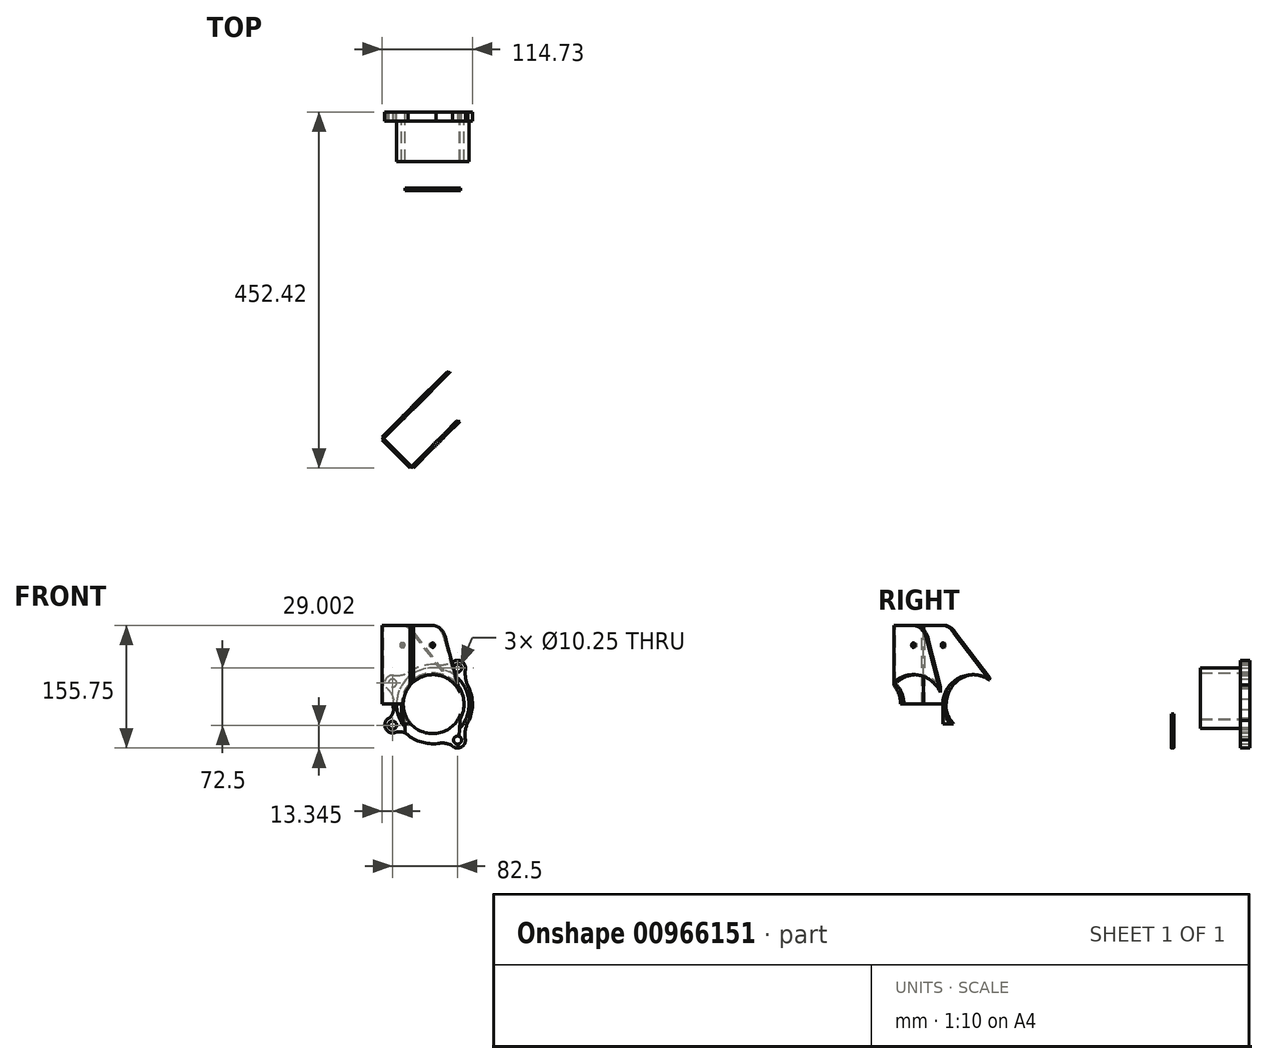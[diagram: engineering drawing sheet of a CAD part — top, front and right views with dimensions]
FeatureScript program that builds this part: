
annotation { "Feature Type Name" : "Feature", "Feature Type Description" : "" }
export const myFeature = defineFeature(function(context is Context, id is Id, definition is map)
    precondition{}
    {
        {
            var Q0;
            Q0=qCreatedBy(makeId("Front.planeOp"),FACE);
            var sketch = newSketch(context, id + "F0", { "sketchPlane" : qUnion([Q0])});
            skLineSegment(sketch, "E0", {"start": v(-45.88, 158.06) * mm, "end": v(-45.88, 92.8) * mm});
            skPoint(sketch, "E1.orphan", {"position": v(-70.88, 8.06) * mm});
            skPoint(sketch, "E2.top.start.orphan", {"position": v(-45.88, 8.06) * mm});
            skPoint(sketch, "E3.orphan", {"position": v(-20.88, 8.06) * mm});
            skLineSegment(sketch, "E4", {"start": v(-45.88, 158.06) * mm, "end": v(-45.88, 212.33) * mm, "construction": true});
            skCircle(sketch, "E5", {"center": v(-45.88, 212.33) * mm, "radius": 39.75 * mm});
            skCircle(sketch, "E6", {"center": v(-96.88, 239.08) * mm, "radius": 5.13 * mm});
            skCircle(sketch, "E7", {"center": v(-96.88, 185.58) * mm, "radius": 5.12 * mm});
            skLineSegment(sketch, "E8", {"start": v(-45.88, 212.33) * mm, "end": v(-96.88, 212.33) * mm, "construction": true});
            skCircle(sketch, "E9", {"center": v(-14.38, 258.08) * mm, "radius": 5.12 * mm});
            skCircle(sketch, "E10", {"center": v(-14.38, 166.58) * mm, "radius": 5.12 * mm});
            skLineSegment(sketch, "E11", {"start": v(-45.88, 212.33) * mm, "end": v(-14.38, 212.33) * mm, "construction": true});
            skLineSegment(sketch, "E12", {"start": v(-96.88, 239.08) * mm, "end": v(-96.88, 185.58) * mm, "construction": true});
            skLineSegment(sketch, "E13", {"start": v(-14.38, 258.08) * mm, "end": v(-14.38, 166.58) * mm, "construction": true});
            skCircle(sketch, "E14", {"center": v(-45.88, 212.33) * mm, "radius": 37.5 * mm});
            skCircle(sketch, "E15", {"center": v(-45.88, 212.33) * mm, "radius": 36 * mm});
            skArc(sketch, "E16", {"start": v(-4.44, 256.92) * mm, "mid": v(-9.67, 266.9) * mm, "end": v(-20.88, 265.68) * mm});
            skArc(sketch, "E17", {"start": v(-95.78, 249.02) * mm, "mid": v(-105.75, 243.7) * mm, "end": v(-104.38, 232.48) * mm});
            skArc(sketch, "E18", {"start": v(-101.31, 194.54) * mm, "mid": v(-105.87, 181.22) * mm, "end": v(-92.6, 176.55) * mm});
            skArc(sketch, "E19", {"start": v(-21.82, 159.91) * mm, "mid": v(-9.65, 157.77) * mm, "end": v(-4.7, 169.09) * mm});
            skArc(sketch, "E20", {"start": v(-39.34, 262.3) * mm, "mid": v(-59.48, 260.85) * mm, "end": v(-77.44, 251.6) * mm});
            skArc(sketch, "E21.trimOffspring", {"start": v(-95.78, 219.27) * mm, "mid": v(-96.26, 212.33) * mm, "end": v(-95.78, 205.4) * mm});
            skArc(sketch, "E22.trimOffspring", {"start": v(-78.83, 174.21) * mm, "mid": v(-59.11, 163.72) * mm, "end": v(-36.8, 162.77) * mm});
            skArc(sketch, "E23.trimOffspring", {"start": v(-2.07, 187.43) * mm, "mid": v(4.51, 212.12) * mm, "end": v(-1.86, 236.86) * mm});
            skArc(sketch, "E24", {"start": v(-4.44, 256.92) * mm, "mid": v(-4.39, 246.73) * mm, "end": v(-1.86, 236.86) * mm});
            skArc(sketch, "E25", {"start": v(0, 191.5) * mm, "mid": v(-4.4, 179.69) * mm, "end": v(-4.39, 167.09) * mm});
            skArc(sketch, "E26", {"start": v(-21.82, 159.91) * mm, "mid": v(-30.43, 162.66) * mm, "end": v(-39.45, 162.36) * mm});
            skArc(sketch, "E27", {"start": v(-78.83, 174.21) * mm, "mid": v(-85.42, 177.1) * mm, "end": v(-92.6, 176.55) * mm});
            skArc(sketch, "E28", {"start": v(-101.31, 194.54) * mm, "mid": v(-97.46, 199.42) * mm, "end": v(-95.78, 205.4) * mm});
            skArc(sketch, "E29", {"start": v(-95.78, 219.27) * mm, "mid": v(-98.85, 226.67) * mm, "end": v(-104.38, 232.48) * mm});
            skArc(sketch, "E30", {"start": v(-95.78, 249.02) * mm, "mid": v(-86.45, 249.18) * mm, "end": v(-77.44, 251.6) * mm});
            skArc(sketch, "E31", {"start": v(-41.62, 262.54) * mm, "mid": v(-31.02, 262.6) * mm, "end": v(-20.88, 265.68) * mm});
            skCircle(sketch, "E32", {"center": v(-45.88, 212.33) * mm, "radius": 46 * mm});
            skLineSegment(sketch, "E33", {"start": v(-45.88, 174.83) * mm, "end": v(-45.88, 124.83) * mm});
            skCircle(sketch, "E34", {"center": v(-45.88, 124.83) * mm, "radius": 6 * mm});
            skPoint(sketch, "E35.center.orphan", {"position": v(-45.88, 113.06) * mm});
            skLineSegment(sketch, "E36", {"start": v(-70.88, 181.43) * mm, "end": v(-70.88, 184.38) * mm});
            skLineSegment(sketch, "E37", {"start": v(-20.88, 158.06) * mm, "end": v(-20.88, 158.98) * mm});
            skLineSegment(sketch, "E38", {"start": v(-45.88, 124.83) * mm, "end": v(-45.88, 99.83) * mm});
            skPoint(sketch, "E39.center.orphan", {"position": v(-45.88, 88.06) * mm});
            skCircle(sketch, "E40", {"center": v(-45.88, 99.83) * mm, "radius": 6 * mm});
            skLineSegment(sketch, "E41", {"start": v(-45.88, 99.83) * mm, "end": v(-45.88, 92.8) * mm});
            skCircle(sketch, "E42", {"center": v(-45.88, 74.83) * mm, "radius": 6 * mm});
            skArc(sketch, "E43", {"start": v(-45.88, 49.83) * mm, "mid": v(-28.2, 57.15) * mm, "end": v(-20.88, 74.83) * mm});
            skLineSegment(sketch, "E44", {"start": v(-45.88, 124.83) * mm, "end": v(-80.88, 124.83) * mm});
            skLineSegment(sketch, "E45", {"start": v(-80.88, 124.83) * mm, "end": v(-80.88, 74.83) * mm});
            skLineSegment(sketch, "E46", {"start": v(-80.88, 124.83) * mm, "end": v(-80.88, 198.87) * mm});
            skPoint(sketch, "E2.left.start.orphan", {"position": v(-70.88, 158.06) * mm});
            skLineSegment(sketch, "E47", {"start": v(-55.88, 49.83) * mm, "end": v(-45.88, 49.83) * mm});
            skLineSegment(sketch, "E48", {"start": v(-45.88, 49.83) * mm, "end": v(-55.88, 49.83) * mm});
            skArc(sketch, "E49", {"start": v(-80.88, 74.83) * mm, "mid": v(-73.55, 57.15) * mm, "end": v(-55.88, 49.83) * mm});
            skLineSegment(sketch, "E50.trimOffspring", {"start": v(-45.88, 80.83) * mm, "end": v(-45.88, 74.83) * mm});
            skLineSegment(sketch, "E51.trimOffspring", {"start": v(-45.88, 88.06) * mm, "end": v(-45.88, 74.83) * mm});
            skLineSegment(sketch, "E52", {"start": v(-10.45, 200.03) * mm, "end": v(-20.88, 74.83) * mm});
            skLineSegment(sketch, "E53.trimOffspring", {"start": v(-20.88, 181.43) * mm, "end": v(-20.88, 184.38) * mm});
            skSolve(sketch);
        }
        {
            var Q0;
            Q0=makeQuery(id+"F0.imprint","IMPRINT",FACE,{"disambiguationData":[TD([[makeQuery(id+"F0.imprint","IMPRINT",EDGE,{"derivedFrom":sQuery(id+"F0.wireOp",EDGE,"E14")}),1.0]])]});
            extrude(context, id + "F1", {"entities" : qUnion([Q0]), "depth" : 400 * mm, "offsetDistance" : 25 * mm});
        }
        {
            var Q0;
            Q0=sQuery(id+"F0.wireOp",VERTEX,"E4.end");
            var Q1;
            Q1=sQuery(id+"F0.wireOp",EDGE,"E11");
            cPlane(context, id + "F2", {"entities" : qUnion([Q0, Q1]), "cplaneType" : CPlaneType.LINE_POINT, "offset" : 25 * mm, "width" : 150 * mm, "height" : 150 * mm});
        }
        {
            var Q0;
            Q0=qCreatedBy(id+"F2.planeOp",FACE);
            var sketch = newSketch(context, id + "F3", { "sketchPlane" : qUnion([Q0])});
            skLineSegment(sketch, "E54", {"start": v(0, 212.33) * mm, "end": v(-611, 212.33) * mm});
            skCircle(sketch, "E55", {"center": v(-611, 212.33) * mm, "radius": 66.24 * mm});
            skLineSegment(sketch, "E56", {"start": v(-427.67, 212.33) * mm, "end": v(-427.67, 287.33) * mm});
            skLineSegment(sketch, "E57", {"start": v(-395.17, 281.83) * mm, "end": v(-395.17, 235.86) * mm});
            skLineSegment(sketch, "E58", {"start": v(-427.67, 212.33) * mm, "end": v(-427.67, 249.83) * mm});
            skLineSegment(sketch, "E59", {"start": v(-427.67, 249.83) * mm, "end": v(-370.95, 249.83) * mm});
            skLineSegment(sketch, "E60", {"start": v(-427.67, 249.83) * mm, "end": v(-427.67, 281.83) * mm});
            skLineSegment(sketch, "E61", {"start": v(-427.67, 281.83) * mm, "end": v(-395.17, 281.83) * mm});
            skSolve(sketch);
        }
        {
            var Q0;
            Q0=makeQuery(id+"F0.imprint","IMPRINT",FACE,{"disambiguationData":[TD([[makeQuery(id+"F0.imprint","IMPRINT",EDGE,{"derivedFrom":sQuery(id+"F0.wireOp",EDGE,"E6")}),-1.0]])]});
            var Q1;
            {var subQ1=sQuery(id+"F0.wireOp",EDGE,"E22.trimOffspring");var subQ7=sQuery(id+"F0.wireOp",EDGE,"E27");var subQ8=makeQuery(id+"F0.imprint","INTERSECT",VERTEX,{"derivedFrom":[subQ1,subQ7]});Q1=makeQuery(id+"F0.imprint","IMPRINT",FACE,{"disambiguationData":[TD([[makeQuery(id+"F0.imprint","IMPRINT",EDGE,{"disambiguationData":[TD([[subQ8,-1.0]])],"derivedFrom":subQ1}),1.0]])]});}
            var Q2;
            {var subQ7=sQuery(id+"F0.wireOp",EDGE,"E19");var subQ8=makeQuery(id+"F0.imprint","IMPRINT",VERTEX,{"derivedFrom":subQ7});Q2=makeQuery(id+"F0.imprint","IMPRINT",FACE,{"disambiguationData":[TD([[makeQuery(id+"F0.imprint","IMPRINT",EDGE,{"disambiguationData":[TD([[subQ8,1.0]])],"derivedFrom":subQ7}),1.0]])]});}
            extrude(context, id + "F4", {"entities" : qUnion([Q0, Q1, Q2]), "depth" : 12 * mm, "offsetDistance" : 25 * mm});
        }
        {
            var Q0;
            Q0=makeQuery(id+"F0.imprint","IMPRINT",FACE,{"disambiguationData":[TD([[makeQuery(id+"F0.imprint","IMPRINT",EDGE,{"derivedFrom":sQuery(id+"F0.wireOp",EDGE,"E14")}),1.0]])]});
            extrude(context, id + "F5", {"entities" : qUnion([Q0]), "operationType" : NewBodyOperationType.REMOVE, "depth" : 136 * mm, "offsetDistance" : 25 * mm});
        }
        {
            var Q0;
            Q0=makeQuery(id+"F0.imprint","IMPRINT",FACE,{"disambiguationData":[TD([[makeQuery(id+"F0.imprint","IMPRINT",EDGE,{"derivedFrom":sQuery(id+"F0.wireOp",EDGE,"E5")}),-1.0]])]});
            var Q1;
            {var subQ0=sQuery(id+"F0.wireOp",EDGE,"E46");var subQ1=sQuery(id+"F0.wireOp",EDGE,"E5");var subQ2=makeQuery(id+"F0.imprint","INTERSECT",VERTEX,{"derivedFrom":[subQ1,subQ0]});Q1=makeQuery(id+"F0.imprint","IMPRINT",FACE,{"disambiguationData":[TD([[makeQuery(id+"F0.imprint","IMPRINT",EDGE,{"disambiguationData":[TD([[subQ2,1.0]])],"derivedFrom":subQ1}),-1.0]])]});}
            extrude(context, id + "F6", {"entities" : qUnion([Q0, Q1]), "depth" : 63 * mm, "offsetDistance" : 25 * mm});
        }
        {
            var Q0;
            Q0=makeQuery(id+"F6.opExtrude","CAP_FACE",FACE,{"disambiguationData":[OSD([sQuery(id+"F0.wireOp",EDGE,"E5"),sQuery(id+"F0.wireOp",EDGE,"E32")])],"isStart":true});
            extrude(context, id + "F7", {"entities" : qUnion([Q0]), "operationType" : NewBodyOperationType.REMOVE, "oppositeDirection" : true, "depth" : 12 * mm, "offsetDistance" : 25 * mm});
        }
        {
            var Q0;
            Q0=sQuery(id+"F3.wireOp",EDGE,"E56");
            var Q1;
            Q1=sQuery(id+"F3.wireOp",VERTEX,"E56.end");
            cPlane(context, id + "F8", {"entities" : qUnion([Q0, Q1]), "cplaneType" : CPlaneType.LINE_POINT, "offset" : 25 * mm, "width" : 150 * mm, "height" : 150 * mm});
        }
        {
            var Q0;
            Q0=qCreatedBy(id+"F8.planeOp",FACE);
            var sketch = newSketch(context, id + "F9", { "sketchPlane" : qUnion([Q0])});
            skLineSegment(sketch, "E62", {"start": v(-45.88, -427.67) * mm, "end": v(-7.54, -427.67) * mm});
            skLineSegment(sketch, "E63", {"start": v(-45.88, -427.67) * mm, "end": v(-45.88, -449.04) * mm});
            skLineSegment(sketch, "E64", {"start": v(-45.88, -427.67) * mm, "end": v(-33.51, -440.03) * mm});
            skLineSegment(sketch, "E65", {"start": v(-48, -425.55) * mm, "end": v(-83.35, -390.2) * mm});
            skLineSegment(sketch, "E66", {"start": v(-83.35, -390.2) * mm, "end": v(-47.41, -354.25) * mm});
            skLineSegment(sketch, "E67", {"start": v(-47.41, -354.25) * mm, "end": v(-83.35, -390.2) * mm});
            skLineSegment(sketch, "E68", {"start": v(-85.47, -388.07) * mm, "end": v(6.45, -296.14) * mm});
            skLineSegment(sketch, "E69", {"start": v(-47.41, -354.25) * mm, "end": v(8.57, -298.27) * mm});
            skLineSegment(sketch, "E70", {"start": v(-48, -425.55) * mm, "end": v(22.71, -354.83) * mm});
            skLineSegment(sketch, "E71", {"start": v(-83.35, -390.2) * mm, "end": v(-12.64, -319.48) * mm});
            skLineSegment(sketch, "E72", {"start": v(-12.64, -319.48) * mm, "end": v(22.71, -354.83) * mm});
            skLineSegment(sketch, "E73", {"start": v(46.04, -335.73) * mm, "end": v(43.92, -333.61) * mm});
            skLineSegment(sketch, "E74", {"start": v(22.7, -354.83) * mm, "end": v(43.92, -333.61) * mm});
            skLineSegment(sketch, "E75", {"start": v(46.04, -335.73) * mm, "end": v(6.45, -296.14) * mm});
            skLineSegment(sketch, "E76", {"start": v(-45.88, -427.67) * mm, "end": v(-48, -425.55) * mm});
            skLineSegment(sketch, "E77.trimOffspring", {"start": v(-83.35, -390.2) * mm, "end": v(-85.47, -388.07) * mm});
            skPoint(sketch, "E78.end.orphan", {"position": v(-58.24, -440.03) * mm});
            skLineSegment(sketch, "E79", {"start": v(-45.88, -427.67) * mm, "end": v(46.04, -335.73) * mm});
            skLineSegment(sketch, "E80", {"start": v(-85.47, -388.07) * mm, "end": v(-110.22, -412.82) * mm});
            skLineSegment(sketch, "E81", {"start": v(-110.22, -412.82) * mm, "end": v(-108.1, -414.94) * mm});
            skLineSegment(sketch, "E82", {"start": v(-108.1, -414.94) * mm, "end": v(-83.35, -390.2) * mm});
            skLineSegment(sketch, "E83", {"start": v(-48, -425.55) * mm, "end": v(-72.74, -450.3) * mm});
            skLineSegment(sketch, "E84", {"start": v(-72.74, -450.3) * mm, "end": v(-70.62, -452.42) * mm});
            skLineSegment(sketch, "E85", {"start": v(-70.62, -452.42) * mm, "end": v(-45.88, -427.67) * mm});
            skLineSegment(sketch, "E86", {"start": v(-72.74, -450.3) * mm, "end": v(-108.1, -414.94) * mm});
            skLineSegment(sketch, "E87", {"start": v(-108.1, -414.94) * mm, "end": v(-110.22, -417.06) * mm});
            skLineSegment(sketch, "E88", {"start": v(-72.74, -450.3) * mm, "end": v(-74.86, -452.42) * mm});
            skLineSegment(sketch, "E89", {"start": v(-74.86, -452.42) * mm, "end": v(-110.22, -417.06) * mm});
            skSolve(sketch);
        }
        {
            var Q0;
            {var subQ4=sQuery(id+"F9.wireOp",EDGE,"E68");Q0=makeQuery(id+"F9.imprint","IMPRINT",FACE,{"disambiguationData":[TD([[makeQuery(id+"F9.imprint","IMPRINT",EDGE,{"derivedFrom":subQ4}),-1.0]])]});}
            var Q1;
            {var subQ4=sQuery(id+"F9.wireOp",EDGE,"E70");Q1=makeQuery(id+"F9.imprint","IMPRINT",FACE,{"disambiguationData":[TD([[makeQuery(id+"F9.imprint","IMPRINT",EDGE,{"derivedFrom":subQ4}),-1.0]])]});}
            extrude(context, id + "F10", {"entities" : qUnion([Q0, Q1]), "oppositeDirection" : true, "depth" : 100 * mm, "offsetDistance" : 25 * mm});
        }
        {
            var Q0;
            Q0=makeQuery(id+"F10.opExtrude","SWEPT_FACE",FACE,{"disambiguationData":[OSD([sQuery(id+"F9.wireOp",EDGE,"E74")])]});
            var sketch = newSketch(context, id + "F11", { "sketchPlane" : qUnion([Q0])});
            skLineSegment(sketch, "E90", {"start": v(234.84, 287.33) * mm, "end": v(234.84, 257.33) * mm});
            skCircle(sketch, "E91", {"center": v(234.84, 257.33) * mm, "radius": 7 * mm});
            skLineSegment(sketch, "E92", {"start": v(234.84, 257.33) * mm, "end": v(234.84, 287.33) * mm});
            skLineSegment(sketch, "E93", {"start": v(234.84, 287.33) * mm, "end": v(334.84, 287.33) * mm});
            skLineSegment(sketch, "E94", {"start": v(204.84, 247.6) * mm, "end": v(19.25, 190.9) * mm});
            skCircle(sketch, "E95", {"center": v(234.84, 257.33) * mm, "radius": 25 * mm});
            skLineSegment(sketch, "E96", {"start": v(245.66, 279.87) * mm, "end": v(334.84, 249.83) * mm});
            skLineSegment(sketch, "E97", {"start": v(290.93, 187.33) * mm, "end": v(204.84, 187.33) * mm});
            skLineSegment(sketch, "E98", {"start": v(334.84, 249.83) * mm, "end": v(334.84, 287.33) * mm});
            skLineSegment(sketch, "E99", {"start": v(221.99, 235.9) * mm, "end": v(290.93, 187.33) * mm});
            skLineSegment(sketch, "E100", {"start": v(204.84, 187.33) * mm, "end": v(204.84, 287.33) * mm});
            skLineSegment(sketch, "E101", {"start": v(204.84, 287.33) * mm, "end": v(334.84, 287.33) * mm});
            skSolve(sketch);
        }
        {
            var Q0;
            {var subQ9=sQuery(id+"F11.wireOp",EDGE,"E100");var subQ13=makeQuery(id+"F11.imprint","IMPRINT",VERTEX,{"derivedFrom":subQ9});Q0=makeQuery(id+"F11.imprint","IMPRINT",FACE,{"disambiguationData":[TD([[makeQuery(id+"F11.imprint","IMPRINT",EDGE,{"disambiguationData":[TD([[subQ13,1.0]])],"derivedFrom":subQ9}),-1.0]])]});}
            var Q1;
            {var subQ0=sQuery(id+"F11.wireOp",EDGE,"E97");var subQ1=sQuery(id+"F11.wireOp",EDGE,"E99");var subQ2=makeQuery(id+"F11.imprint","INTERSECT",VERTEX,{"derivedFrom":[subQ1,subQ0]});Q1=makeQuery(id+"F11.imprint","IMPRINT",FACE,{"disambiguationData":[TD([[makeQuery(id+"F11.imprint","IMPRINT",EDGE,{"disambiguationData":[TD([[subQ2,1.0]])],"derivedFrom":subQ1}),-1.0]])]});}
            var Q2;
            {var subQ1=sQuery(id+"F11.wireOp",EDGE,"E96");Q2=makeQuery(id+"F11.imprint","IMPRINT",FACE,{"disambiguationData":[TD([[makeQuery(id+"F11.imprint","IMPRINT",EDGE,{"derivedFrom":subQ1}),1.0]])]});}
            extrude(context, id + "F12", {"entities" : qUnion([Q0, Q1, Q2]), "operationType" : NewBodyOperationType.REMOVE, "depth" : 80.2 * mm, "offsetDistance" : 25 * mm});
        }
        {
            var Q0;
            {var subQ9=sQuery(id+"F11.wireOp",EDGE,"E100");var subQ13=makeQuery(id+"F11.imprint","IMPRINT",VERTEX,{"derivedFrom":subQ9});Q0=makeQuery(id+"F11.imprint","IMPRINT",FACE,{"disambiguationData":[TD([[makeQuery(id+"F11.imprint","IMPRINT",EDGE,{"disambiguationData":[TD([[subQ13,1.0]])],"derivedFrom":subQ9}),-1.0]])]});}
            var Q1;
            {var subQ0=sQuery(id+"F11.wireOp",EDGE,"E97");var subQ1=sQuery(id+"F11.wireOp",EDGE,"E99");var subQ2=makeQuery(id+"F11.imprint","INTERSECT",VERTEX,{"derivedFrom":[subQ1,subQ0]});Q1=makeQuery(id+"F11.imprint","IMPRINT",FACE,{"disambiguationData":[TD([[makeQuery(id+"F11.imprint","IMPRINT",EDGE,{"disambiguationData":[TD([[subQ2,1.0]])],"derivedFrom":subQ1}),-1.0]])]});}
            var Q2;
            {var subQ1=sQuery(id+"F11.wireOp",EDGE,"E96");Q2=makeQuery(id+"F11.imprint","IMPRINT",FACE,{"disambiguationData":[TD([[makeQuery(id+"F11.imprint","IMPRINT",EDGE,{"derivedFrom":subQ1}),1.0]])]});}
            extrude(context, id + "F13", {"entities" : qUnion([Q0, Q1, Q2]), "operationType" : NewBodyOperationType.REMOVE, "oppositeDirection" : true, "depth" : 25 * mm, "offsetDistance" : 25 * mm});
        }
        {
            var Q0;
            {var subQ0=sQuery(id+"F11.wireOp",EDGE,"E92");var subQ1=sQuery(id+"F11.wireOp",EDGE,"E91");var subQ2=makeQuery(id+"F11.imprint","INTERSECT",VERTEX,{"derivedFrom":[subQ1,subQ0]});Q0=makeQuery(id+"F11.imprint","IMPRINT",FACE,{"disambiguationData":[TD([[makeQuery(id+"F11.imprint","IMPRINT",EDGE,{"disambiguationData":[TD([[subQ2,1.0]])],"derivedFrom":subQ1}),1.0]])]});}
            var Q1;
            {var subQ0=sQuery(id+"F11.wireOp",EDGE,"E92");var subQ1=sQuery(id+"F11.wireOp",EDGE,"E91");var subQ2=makeQuery(id+"F11.imprint","INTERSECT",VERTEX,{"derivedFrom":[subQ1,subQ0]});Q1=makeQuery(id+"F11.imprint","IMPRINT",FACE,{"disambiguationData":[TD([[makeQuery(id+"F11.imprint","IMPRINT",EDGE,{"disambiguationData":[TD([[subQ2,-1.0]])],"derivedFrom":subQ1}),1.0]])]});}
            var Q2;
            Q2=sQuery(id+"F11.wireOp",EDGE,"E91");
            extrude(context, id + "F14", {"entities" : qUnion([Q0, Q1]), "operationType" : NewBodyOperationType.REMOVE, "surfaceEntities" : qUnion([Q2]), "depth" : 58.2 * mm, "offsetDistance" : 25 * mm});
        }
        {
            var Q0;
            {var subQ0=sQuery(id+"F11.wireOp",EDGE,"E92");var subQ1=sQuery(id+"F11.wireOp",EDGE,"E91");var subQ2=makeQuery(id+"F11.imprint","INTERSECT",VERTEX,{"derivedFrom":[subQ1,subQ0]});Q0=makeQuery(id+"F11.imprint","IMPRINT",FACE,{"disambiguationData":[TD([[makeQuery(id+"F11.imprint","IMPRINT",EDGE,{"disambiguationData":[TD([[subQ2,-1.0]])],"derivedFrom":subQ1}),1.0]])]});}
            var Q1;
            {var subQ0=sQuery(id+"F11.wireOp",EDGE,"E92");var subQ1=sQuery(id+"F11.wireOp",EDGE,"E91");var subQ2=makeQuery(id+"F11.imprint","INTERSECT",VERTEX,{"derivedFrom":[subQ1,subQ0]});Q1=makeQuery(id+"F11.imprint","IMPRINT",FACE,{"disambiguationData":[TD([[makeQuery(id+"F11.imprint","IMPRINT",EDGE,{"disambiguationData":[TD([[subQ2,1.0]])],"derivedFrom":subQ1}),1.0]])]});}
            extrude(context, id + "F15", {"entities" : qUnion([Q0, Q1]), "operationType" : NewBodyOperationType.REMOVE, "oppositeDirection" : true, "depth" : 25 * mm, "offsetDistance" : 25 * mm});
        }
        {
            var Q0;
            Q0=makeQuery(id+"F0.imprint","IMPRINT",FACE,{"disambiguationData":[TD([[makeQuery(id+"F0.imprint","IMPRINT",EDGE,{"derivedFrom":sQuery(id+"F0.wireOp",EDGE,"E14")}),1.0]])]});
            var Q1;
            Q1=sQuery(id+"F0.wireOp",EDGE,"E15");
            var Q2;
            Q2=sQuery(id+"F0.wireOp",EDGE,"E14");
            extrude(context, id + "F16", {"entities" : qUnion([Q0]), "operationType" : NewBodyOperationType.REMOVE, "surfaceEntities" : qUnion([Q1, Q2]), "depth" : 641 * mm, "offsetDistance" : 25 * mm});
        }
        {
            var Q0;
            {var subQ0=sQuery(id+"F9.wireOp",EDGE,"E71");var subQ1=sQuery(id+"F9.wireOp",EDGE,"E69");Q0=makeQuery(id+"F16.boolean.opBoolean","SPLIT",FACE,{"disambiguationData":[TD([makeQuery(id+"F10.opExtrude","CAP_FACE",FACE,{"disambiguationData":[OSD([sQuery(id+"F9.wireOp",EDGE,"E68"),subQ1,subQ0,sQuery(id+"F9.wireOp",EDGE,"E75"),sQuery(id+"F9.wireOp",EDGE,"E77.trimOffspring")])],"isStart":false}),makeQuery(id+"F12.boolean.opBoolean","COPY",FACE,{"derivedFrom":makeQuery(id+"F12.opExtrude","SWEPT_FACE",FACE,{"disambiguationData":[OSD([sQuery(id+"F11.wireOp",EDGE,"E99")])]})}),makeQuery(id+"F16.opExtrude","SWEPT_FACE",FACE,{"disambiguationData":[OSD([sQuery(id+"F0.wireOp",EDGE,"E15")])]})])],"derivedFrom":makeQuery(id+"F10.opExtrude","SWEPT_FACE",FACE,{"disambiguationData":[OSD([subQ1,subQ0])]})});}
            extrude(context, id + "F17", {"entities" : qUnion([Q0]), "operationType" : NewBodyOperationType.REMOVE, "oppositeDirection" : true, "depth" : 25 * mm, "offsetDistance" : 25 * mm});
        }
        {
            var Q0;
            Q0=makeQuery(id+"F0.imprint","IMPRINT",FACE,{"disambiguationData":[TD([[makeQuery(id+"F0.imprint","IMPRINT",EDGE,{"derivedFrom":sQuery(id+"F0.wireOp",EDGE,"E15")}),1.0]])]});
            extrude(context, id + "F18", {"entities" : qUnion([Q0]), "operationType" : NewBodyOperationType.REMOVE, "depth" : 770 * mm, "offsetDistance" : 25 * mm});
        }
        {
            var Q0;
            Q0=makeQuery(id+"F9.imprint","IMPRINT",FACE,{"disambiguationData":[TD([[makeQuery(id+"F9.imprint","IMPRINT",EDGE,{"derivedFrom":sQuery(id+"F9.wireOp",EDGE,"E86")}),1.0]])]});
            var Q1;
            Q1=makeQuery(id+"F9.imprint","IMPRINT",FACE,{"disambiguationData":[TD([[makeQuery(id+"F9.imprint","IMPRINT",EDGE,{"derivedFrom":sQuery(id+"F9.wireOp",EDGE,"E76")}),1.0]])]});
            var Q2;
            Q2=makeQuery(id+"F9.imprint","IMPRINT",FACE,{"disambiguationData":[TD([[makeQuery(id+"F9.imprint","IMPRINT",EDGE,{"derivedFrom":sQuery(id+"F9.wireOp",EDGE,"E77.trimOffspring")}),1.0]])]});
            var Q3;
            {var subQ4=sQuery(id+"F9.wireOp",EDGE,"E68");Q3=makeQuery(id+"F9.imprint","IMPRINT",FACE,{"disambiguationData":[TD([[makeQuery(id+"F9.imprint","IMPRINT",EDGE,{"derivedFrom":subQ4}),-1.0]])]});}
            var Q4;
            {var subQ4=sQuery(id+"F9.wireOp",EDGE,"E70");Q4=makeQuery(id+"F9.imprint","IMPRINT",FACE,{"disambiguationData":[TD([[makeQuery(id+"F9.imprint","IMPRINT",EDGE,{"derivedFrom":subQ4}),-1.0]])]});}
            extrude(context, id + "F19", {"entities" : qUnion([Q0, Q1, Q2, Q3, Q4]), "oppositeDirection" : true, "depth" : 75 * mm, "offsetDistance" : 25 * mm});
        }
        {
            var Q0;
            Q0=makeQuery(id+"F0.imprint","IMPRINT",FACE,{"disambiguationData":[TD([[makeQuery(id+"F0.imprint","IMPRINT",EDGE,{"derivedFrom":sQuery(id+"F0.wireOp",EDGE,"E14")}),1.0]])]});
            var Q1;
            Q1=makeQuery(id+"F0.imprint","IMPRINT",FACE,{"disambiguationData":[TD([[makeQuery(id+"F0.imprint","IMPRINT",EDGE,{"derivedFrom":sQuery(id+"F0.wireOp",EDGE,"E15")}),1.0]])]});
            extrude(context, id + "F20", {"entities" : qUnion([Q0, Q1]), "operationType" : NewBodyOperationType.REMOVE, "depth" : 487 * mm, "offsetDistance" : 25 * mm});
        }
        {
            var Q0;
            Q0=makeQuery(id+"F9.imprint","IMPRINT",FACE,{"disambiguationData":[TD([[makeQuery(id+"F9.imprint","IMPRINT",EDGE,{"derivedFrom":sQuery(id+"F9.wireOp",EDGE,"E76")}),1.0]])]});
            var Q1;
            {var subQ4=sQuery(id+"F9.wireOp",EDGE,"E70");Q1=makeQuery(id+"F9.imprint","IMPRINT",FACE,{"disambiguationData":[TD([[makeQuery(id+"F9.imprint","IMPRINT",EDGE,{"derivedFrom":subQ4}),-1.0]])]});}
            extrude(context, id + "F21", {"entities" : qUnion([Q0, Q1]), "operationType" : NewBodyOperationType.ADD, "depth" : 25 * mm, "offsetDistance" : 25 * mm});
        }
        {
            var Q0;
            {var subQ4=sQuery(id+"F9.wireOp",EDGE,"E68");Q0=makeQuery(id+"F9.imprint","IMPRINT",FACE,{"disambiguationData":[TD([[makeQuery(id+"F9.imprint","IMPRINT",EDGE,{"derivedFrom":subQ4}),-1.0]])]});}
            var Q1;
            Q1=makeQuery(id+"F9.imprint","IMPRINT",FACE,{"disambiguationData":[TD([[makeQuery(id+"F9.imprint","IMPRINT",EDGE,{"derivedFrom":sQuery(id+"F9.wireOp",EDGE,"E77.trimOffspring")}),1.0]])]});
            extrude(context, id + "F22", {"entities" : qUnion([Q0, Q1]), "operationType" : NewBodyOperationType.ADD, "depth" : 25 * mm, "offsetDistance" : 25 * mm});
        }
        {
            var Q0;
            Q0=makeQuery(id+"F9.imprint","IMPRINT",FACE,{"disambiguationData":[TD([[makeQuery(id+"F9.imprint","IMPRINT",EDGE,{"derivedFrom":sQuery(id+"F9.wireOp",EDGE,"E86")}),1.0]])]});
            extrude(context, id + "F23", {"entities" : qUnion([Q0]), "operationType" : NewBodyOperationType.ADD, "depth" : 25 * mm, "offsetDistance" : 25 * mm});
        }
        {
            var Q0;
            {var subQ0=sQuery(id+"F9.wireOp",EDGE,"E83");Q0=makeQuery(id+"F21.boolean.opBoolean","MERGE",FACE,{"derivedFrom":[makeQuery(id+"F19.opExtrude","SWEPT_FACE",FACE,{"disambiguationData":[OSD([subQ0])]}),makeQuery(id+"F21.opExtrude","SWEPT_FACE",FACE,{"disambiguationData":[OSD([subQ0])]})]});}
            var sketch = newSketch(context, id + "F24", { "sketchPlane" : qUnion([Q0])});
            skCircle(sketch, "E102", {"center": v(334.87, 287.33) * mm, "radius": 3 * mm});
            skSolve(sketch);
        }
        {
            var Q0;
            Q0 = qSketchRegion(id + "F24", true);
            extrude(context, id + "F25", {"entities" : qUnion([Q0]), "operationType" : NewBodyOperationType.REMOVE, "oppositeDirection" : true, "depth" : 25 * mm, "offsetDistance" : 25 * mm});
        }
        {
            var Q0;
            Q0 = qSketchRegion(id + "F24", true);
            extrude(context, id + "F26", {"entities" : qUnion([Q0]), "operationType" : NewBodyOperationType.REMOVE, "depth" : 128.7 * mm, "offsetDistance" : 25 * mm});
        }
        {
            var Q0;
            {var subQ0=sQuery(id+"F9.wireOp",EDGE,"E85");var subQ1=sQuery(id+"F9.wireOp",EDGE,"E79");Q0=makeQuery(id+"F21.boolean.opBoolean","MERGE",FACE,{"derivedFrom":[makeQuery(id+"F19.opExtrude","SWEPT_FACE",FACE,{"disambiguationData":[OSD([subQ1,subQ0])]}),makeQuery(id+"F21.opExtrude","SWEPT_FACE",FACE,{"disambiguationData":[OSD([subQ1,subQ0])]})]});}
            var sketch = newSketch(context, id + "F27", { "sketchPlane" : qUnion([Q0])});
            skCircle(sketch, "E103", {"center": v(-334.87, 287.33) * mm, "radius": 25 * mm});
            skLineSegment(sketch, "E104", {"start": v(-310.66, 293.54) * mm, "end": v(-286.26, 227.32) * mm});
            skSolve(sketch);
        }
        {
            var Q0;
            {var subQ5=sQuery(id+"F27.wireOp",EDGE,"E104");Q0=makeQuery(id+"F27.imprint","IMPRINT",FACE,{"disambiguationData":[TD([[makeQuery(id+"F27.imprint","IMPRINT",EDGE,{"derivedFrom":subQ5}),1.0]])]});}
            extrude(context, id + "F28", {"entities" : qUnion([Q0]), "operationType" : NewBodyOperationType.REMOVE, "oppositeDirection" : true, "depth" : 25 * mm, "offsetDistance" : 25 * mm});
        }
        {
            var Q0;
            {var subQ0=sQuery(id+"F9.wireOp",EDGE,"E82");var subQ1=sQuery(id+"F9.wireOp",EDGE,"E71");var subQ2=sQuery(id+"F9.wireOp",EDGE,"E69");Q0=makeQuery(id+"F22.boolean.opBoolean","MERGE",FACE,{"derivedFrom":[makeQuery(id+"F19.opExtrude","SWEPT_FACE",FACE,{"disambiguationData":[OSD([subQ2,subQ1,subQ0])]}),makeQuery(id+"F22.opExtrude","SWEPT_FACE",FACE,{"disambiguationData":[OSD([subQ2,subQ1,subQ0])]})]});}
            var sketch = newSketch(context, id + "F29", { "sketchPlane" : qUnion([Q0])});
            skCircle(sketch, "E105", {"center": v(-334.85, 287.33) * mm, "radius": 25 * mm});
            skLineSegment(sketch, "E106", {"start": v(-314.78, 302.23) * mm, "end": v(-250.89, 242.78) * mm});
            skSolve(sketch);
        }
        {
            var Q0;
            {var subQ8=sQuery(id+"F29.wireOp",EDGE,"E106");Q0=makeQuery(id+"F29.imprint","IMPRINT",FACE,{"disambiguationData":[TD([[makeQuery(id+"F29.imprint","IMPRINT",EDGE,{"derivedFrom":subQ8}),1.0]])]});}
            extrude(context, id + "F30", {"entities" : qUnion([Q0]), "operationType" : NewBodyOperationType.REMOVE, "oppositeDirection" : true, "depth" : 25 * mm, "offsetDistance" : 25 * mm});
        }
        {
            var Q0;
            Q0=makeQuery(id+"F0.imprint","IMPRINT",FACE,{"disambiguationData":[TD([[makeQuery(id+"F0.imprint","IMPRINT",EDGE,{"derivedFrom":sQuery(id+"F0.wireOp",EDGE,"E42")}),-1.0]])]});
            var Q1;
            {var subQ0=sQuery(id+"F0.wireOp",EDGE,"E33");var subQ1=makeQuery(id+"F0.imprint","IMPRINT",VERTEX,{"derivedFrom":subQ0});Q1=makeQuery(id+"F0.imprint","IMPRINT",FACE,{"disambiguationData":[TD([[makeQuery(id+"F0.imprint","IMPRINT",EDGE,{"disambiguationData":[TD([[subQ1,1.0]])],"derivedFrom":subQ0}),-1.0]])]});}
            var Q2;
            {var subQ7=sQuery(id+"F0.wireOp",EDGE,"E19");var subQ8=makeQuery(id+"F0.imprint","IMPRINT",VERTEX,{"derivedFrom":subQ7});Q2=makeQuery(id+"F0.imprint","IMPRINT",FACE,{"disambiguationData":[TD([[makeQuery(id+"F0.imprint","IMPRINT",EDGE,{"disambiguationData":[TD([[subQ8,1.0]])],"derivedFrom":subQ7}),1.0]])]});}
            var Q3;
            {var subQ1=sQuery(id+"F0.wireOp",EDGE,"E22.trimOffspring");var subQ7=sQuery(id+"F0.wireOp",EDGE,"E27");var subQ8=makeQuery(id+"F0.imprint","INTERSECT",VERTEX,{"derivedFrom":[subQ1,subQ7]});Q3=makeQuery(id+"F0.imprint","IMPRINT",FACE,{"disambiguationData":[TD([[makeQuery(id+"F0.imprint","IMPRINT",EDGE,{"disambiguationData":[TD([[subQ8,-1.0]])],"derivedFrom":subQ1}),1.0]])]});}
            var Q4;
            {var subQ5=sQuery(id+"F0.wireOp",EDGE,"E5");var subQ7=makeQuery(id+"F0.imprint","INTERSECT",VERTEX,{"derivedFrom":[subQ5,sQuery(id+"F0.wireOp",EDGE,"E53.trimOffspring")]});Q4=makeQuery(id+"F0.imprint","IMPRINT",FACE,{"disambiguationData":[TD([[makeQuery(id+"F0.imprint","IMPRINT",EDGE,{"disambiguationData":[TD([[subQ7,1.0]])],"derivedFrom":subQ5}),-1.0]])]});}
            var Q5;
            {var subQ1=sQuery(id+"F0.wireOp",EDGE,"E5");var subQ7=makeQuery(id+"F0.imprint","INTERSECT",VERTEX,{"derivedFrom":[subQ1,sQuery(id+"F0.wireOp",EDGE,"E36")]});Q5=makeQuery(id+"F0.imprint","IMPRINT",FACE,{"disambiguationData":[TD([[makeQuery(id+"F0.imprint","IMPRINT",EDGE,{"disambiguationData":[TD([[subQ7,1.0]])],"derivedFrom":subQ1}),-1.0]])]});}
            var Q6;
            {var subQ0=sQuery(id+"F0.wireOp",EDGE,"E36");Q6=makeQuery(id+"F0.imprint","IMPRINT",FACE,{"disambiguationData":[TD([[makeQuery(id+"F0.imprint","IMPRINT",EDGE,{"derivedFrom":subQ0}),1.0]])]});}
            var Q7;
            {var subQ0=sQuery(id+"F0.wireOp",EDGE,"E36");Q7=makeQuery(id+"F0.imprint","IMPRINT",FACE,{"disambiguationData":[TD([[makeQuery(id+"F0.imprint","IMPRINT",EDGE,{"derivedFrom":subQ0}),-1.0]])]});}
            var Q8;
            {var subQ0=sQuery(id+"F0.wireOp",EDGE,"E53.trimOffspring");Q8=makeQuery(id+"F0.imprint","IMPRINT",FACE,{"disambiguationData":[TD([[makeQuery(id+"F0.imprint","IMPRINT",EDGE,{"derivedFrom":subQ0}),1.0]])]});}
            var Q9;
            {var subQ0=sQuery(id+"F0.wireOp",EDGE,"E53.trimOffspring");Q9=makeQuery(id+"F0.imprint","IMPRINT",FACE,{"disambiguationData":[TD([[makeQuery(id+"F0.imprint","IMPRINT",EDGE,{"derivedFrom":subQ0}),-1.0]])]});}
            extrude(context, id + "F31", {"entities" : qUnion([Q0, Q1, Q2, Q3, Q4, Q5, Q6, Q7, Q8, Q9]), "depth" : 100 * mm, "offsetDistance" : 25 * mm});
        }
        {
            var Q0;
            {var subQ0=sQuery(id+"F0.wireOp",EDGE,"E33");var subQ1=makeQuery(id+"F0.imprint","IMPRINT",VERTEX,{"derivedFrom":subQ0});Q0=makeQuery(id+"F0.imprint","IMPRINT",FACE,{"disambiguationData":[TD([[makeQuery(id+"F0.imprint","IMPRINT",EDGE,{"disambiguationData":[TD([[subQ1,1.0]])],"derivedFrom":subQ0}),-1.0]])]});}
            var Q1;
            Q1=makeQuery(id+"F0.imprint","IMPRINT",FACE,{"disambiguationData":[TD([[makeQuery(id+"F0.imprint","IMPRINT",EDGE,{"derivedFrom":sQuery(id+"F0.wireOp",EDGE,"E42")}),-1.0]])]});
            var Q2;
            {var subQ7=sQuery(id+"F0.wireOp",EDGE,"E19");var subQ8=makeQuery(id+"F0.imprint","IMPRINT",VERTEX,{"derivedFrom":subQ7});Q2=makeQuery(id+"F0.imprint","IMPRINT",FACE,{"disambiguationData":[TD([[makeQuery(id+"F0.imprint","IMPRINT",EDGE,{"disambiguationData":[TD([[subQ8,1.0]])],"derivedFrom":subQ7}),1.0]])]});}
            var Q3;
            {var subQ5=sQuery(id+"F0.wireOp",EDGE,"E5");var subQ7=makeQuery(id+"F0.imprint","INTERSECT",VERTEX,{"derivedFrom":[subQ5,sQuery(id+"F0.wireOp",EDGE,"E53.trimOffspring")]});Q3=makeQuery(id+"F0.imprint","IMPRINT",FACE,{"disambiguationData":[TD([[makeQuery(id+"F0.imprint","IMPRINT",EDGE,{"disambiguationData":[TD([[subQ7,1.0]])],"derivedFrom":subQ5}),-1.0]])]});}
            var Q4;
            {var subQ1=sQuery(id+"F0.wireOp",EDGE,"E22.trimOffspring");var subQ7=sQuery(id+"F0.wireOp",EDGE,"E27");var subQ8=makeQuery(id+"F0.imprint","INTERSECT",VERTEX,{"derivedFrom":[subQ1,subQ7]});Q4=makeQuery(id+"F0.imprint","IMPRINT",FACE,{"disambiguationData":[TD([[makeQuery(id+"F0.imprint","IMPRINT",EDGE,{"disambiguationData":[TD([[subQ8,-1.0]])],"derivedFrom":subQ1}),1.0]])]});}
            var Q5;
            {var subQ1=sQuery(id+"F0.wireOp",EDGE,"E5");var subQ7=makeQuery(id+"F0.imprint","INTERSECT",VERTEX,{"derivedFrom":[subQ1,sQuery(id+"F0.wireOp",EDGE,"E36")]});Q5=makeQuery(id+"F0.imprint","IMPRINT",FACE,{"disambiguationData":[TD([[makeQuery(id+"F0.imprint","IMPRINT",EDGE,{"disambiguationData":[TD([[subQ7,1.0]])],"derivedFrom":subQ1}),-1.0]])]});}
            var Q6;
            {var subQ0=sQuery(id+"F0.wireOp",EDGE,"E36");Q6=makeQuery(id+"F0.imprint","IMPRINT",FACE,{"disambiguationData":[TD([[makeQuery(id+"F0.imprint","IMPRINT",EDGE,{"derivedFrom":subQ0}),-1.0]])]});}
            var Q7;
            {var subQ0=sQuery(id+"F0.wireOp",EDGE,"E36");Q7=makeQuery(id+"F0.imprint","IMPRINT",FACE,{"disambiguationData":[TD([[makeQuery(id+"F0.imprint","IMPRINT",EDGE,{"derivedFrom":subQ0}),1.0]])]});}
            var Q8;
            {var subQ0=sQuery(id+"F0.wireOp",EDGE,"E53.trimOffspring");Q8=makeQuery(id+"F0.imprint","IMPRINT",FACE,{"disambiguationData":[TD([[makeQuery(id+"F0.imprint","IMPRINT",EDGE,{"derivedFrom":subQ0}),1.0]])]});}
            var Q9;
            {var subQ0=sQuery(id+"F0.wireOp",EDGE,"E53.trimOffspring");Q9=makeQuery(id+"F0.imprint","IMPRINT",FACE,{"disambiguationData":[TD([[makeQuery(id+"F0.imprint","IMPRINT",EDGE,{"derivedFrom":subQ0}),-1.0]])]});}
            var Q10;
            {var subQ0=sQuery(id+"F0.wireOp",EDGE,"E52");var subQ1=sQuery(id+"F0.wireOp",EDGE,"E10");var subQ2=makeQuery(id+"F0.imprint","INTERSECT",VERTEX,{"disambiguationData":[OD(0.0)],"derivedFrom":[subQ1,subQ0]});Q10=makeQuery(id+"F0.imprint","IMPRINT",FACE,{"disambiguationData":[TD([[makeQuery(id+"F0.imprint","IMPRINT",EDGE,{"disambiguationData":[TD([[subQ2,-1.0]])],"derivedFrom":subQ1}),1.0]])]});}
            extrude(context, id + "F32", {"entities" : qUnion([Q0, Q1, Q2, Q3, Q4, Q5, Q6, Q7, Q8, Q9, Q10]), "operationType" : NewBodyOperationType.REMOVE, "depth" : 97 * mm, "offsetDistance" : 25 * mm});
        }
    });
